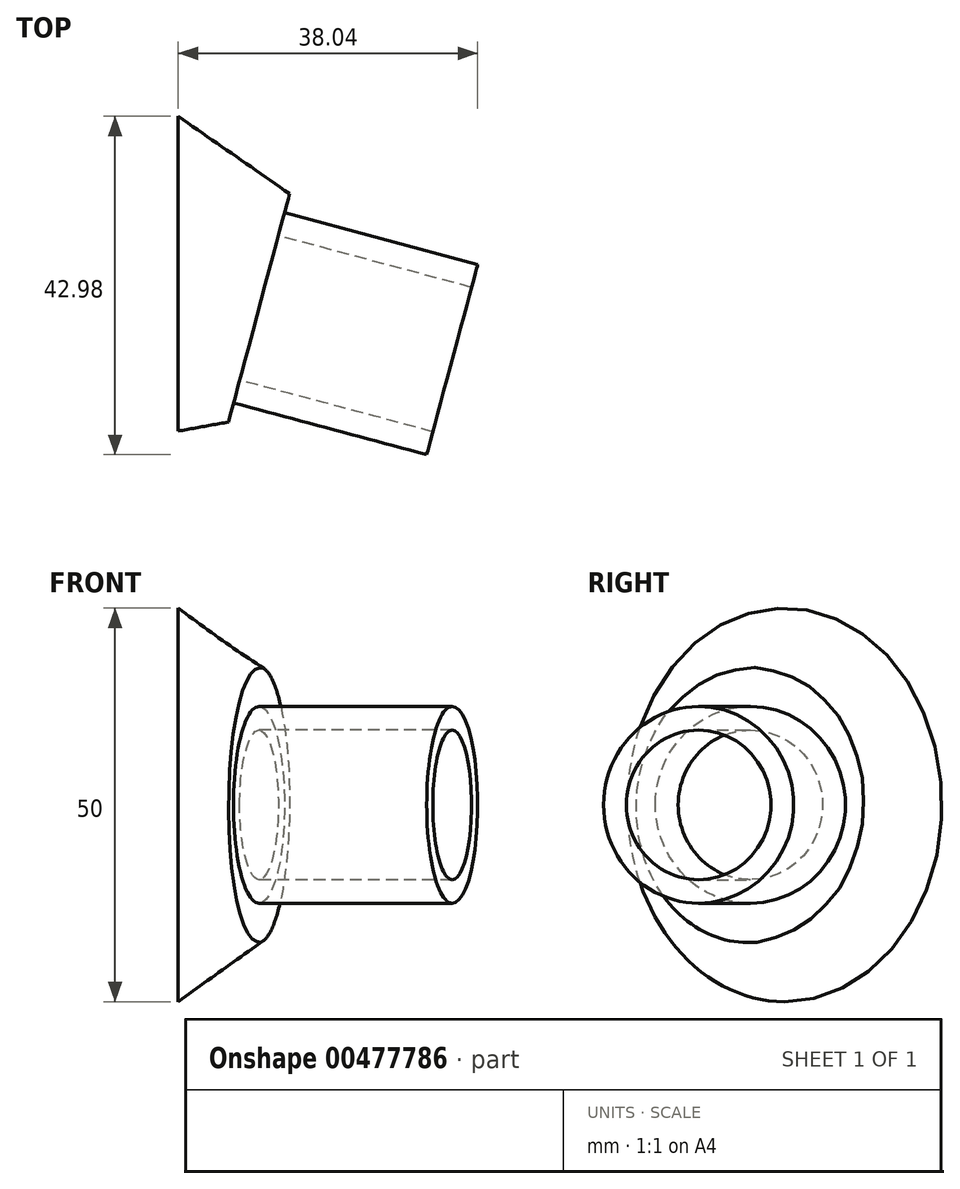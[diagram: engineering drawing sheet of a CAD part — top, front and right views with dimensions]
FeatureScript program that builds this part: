
annotation { "Feature Type Name" : "Feature", "Feature Type Description" : "" }
export const myFeature = defineFeature(function(context is Context, id is Id, definition is map)
    precondition{}
    {
        {
            var Q0;
            Q0=qCreatedBy(makeId("Front.planeOp"),FACE);
            var sketch = newSketch(context, id + "F0", { "sketchPlane" : qUnion([Q0])});
            skLineSegment(sketch, "E0", {"start": v(10.17, 22.95) * mm, "end": v(10.17, -24.03) * mm});
            skSolve(sketch);
        }
        {
            var Q0;
            Q0=sQuery(id+"F0.wireOp",EDGE,"E0");
            cPlane(context, id + "F1", {"entities" : qUnion([Q0]), "cplaneType" : CPlaneType.LINE_ANGLE, "offset" : 25 * mm, "angle" : 15 * degree, "width" : 150 * mm, "height" : 150 * mm});
        }
        {
            var Q0;
            Q0=qCreatedBy(id+"F1.planeOp",FACE);
            var sketch = newSketch(context, id + "F2", { "sketchPlane" : qUnion([Q0])});
            skEllipse(sketch, "E1", {"center": v(-3, 0) * mm, "majorRadius": 17.5 * mm, "minorRadius": 15 * mm, "majorAxis": v(-0.07, 1)});
            skSolve(sketch);
        }
        {
            var Q0;
            Q0=qCreatedBy(id+"F1.planeOp",FACE);
            var sketch = newSketch(context, id + "F3", { "sketchPlane" : qUnion([Q0])});
            skCircle(sketch, "E2", {"center": v(-3, 0) * mm, "radius": 12.5 * mm});
            skSolve(sketch);
        }
        {
            var Q0;
            Q0=qSketchRegion(id+"F3",true);
            extrude(context, id + "F4", {"entities" : qUnion([Q0]), "oppositeDirection" : true, "depth" : 25.4 * mm, "offsetDistance" : 25 * mm});
        }
        {
            var Q0;
            Q0=qCreatedBy(makeId("Right.planeOp"),FACE);
            var sketch = newSketch(context, id + "F5", { "sketchPlane" : qUnion([Q0])});
            skEllipse(sketch, "E3", {"center": v(4.7, 0) * mm, "majorRadius": 25 * mm, "minorRadius": 20 * mm, "majorAxis": v(0, -1)});
            skSolve(sketch);
        }
        {
            var Q1;
            Q1=makeQuery(id+"F5.imprint","IMPRINT",FACE,{"disambiguationData":[TD([[makeQuery(id+"F5.imprint","IMPRINT",EDGE,{"derivedFrom":sQuery(id+"F5.wireOp",EDGE,"E3")}),1.0]])]});
            var Q2;
            Q2=makeQuery(id+"F2.imprint","IMPRINT",FACE,{"disambiguationData":[TD([[makeQuery(id+"F2.imprint","IMPRINT",EDGE,{"derivedFrom":sQuery(id+"F2.wireOp",EDGE,"E1")}),1.0]])]});
            loft(context, id + "F6", {"operationType" : NewBodyOperationType.ADD, "sheetProfilesArray" : [{ "sheetProfileEntities" : qUnion([Q1]) }, { "sheetProfileEntities" : qUnion([Q2]) }]});
        }
        {
            var Q0;
            Q0=sQuery(id+"F3.wireOp",VERTEX,"E2.center");
            var Q1;
            Q1=makeQuery(id+"F4.opExtrude","SWEPT_BODY",BODY,{"disambiguationData":[OSD([sQuery(id+"F3.wireOp",EDGE,"E2")])]});
            hole(context, id + "F7", {"style" : HoleStyle.SIMPLE, "endStyle" : HoleEndStyle.THROUGH, "holeDiameter" : 19 * mm, "isTappedThrough" : true, "tappedDepth" : 12 * mm, "tapClearance" : 3, "locations" : qUnion([Q0]), "scope" : qUnion([Q1])});
        }
    });
